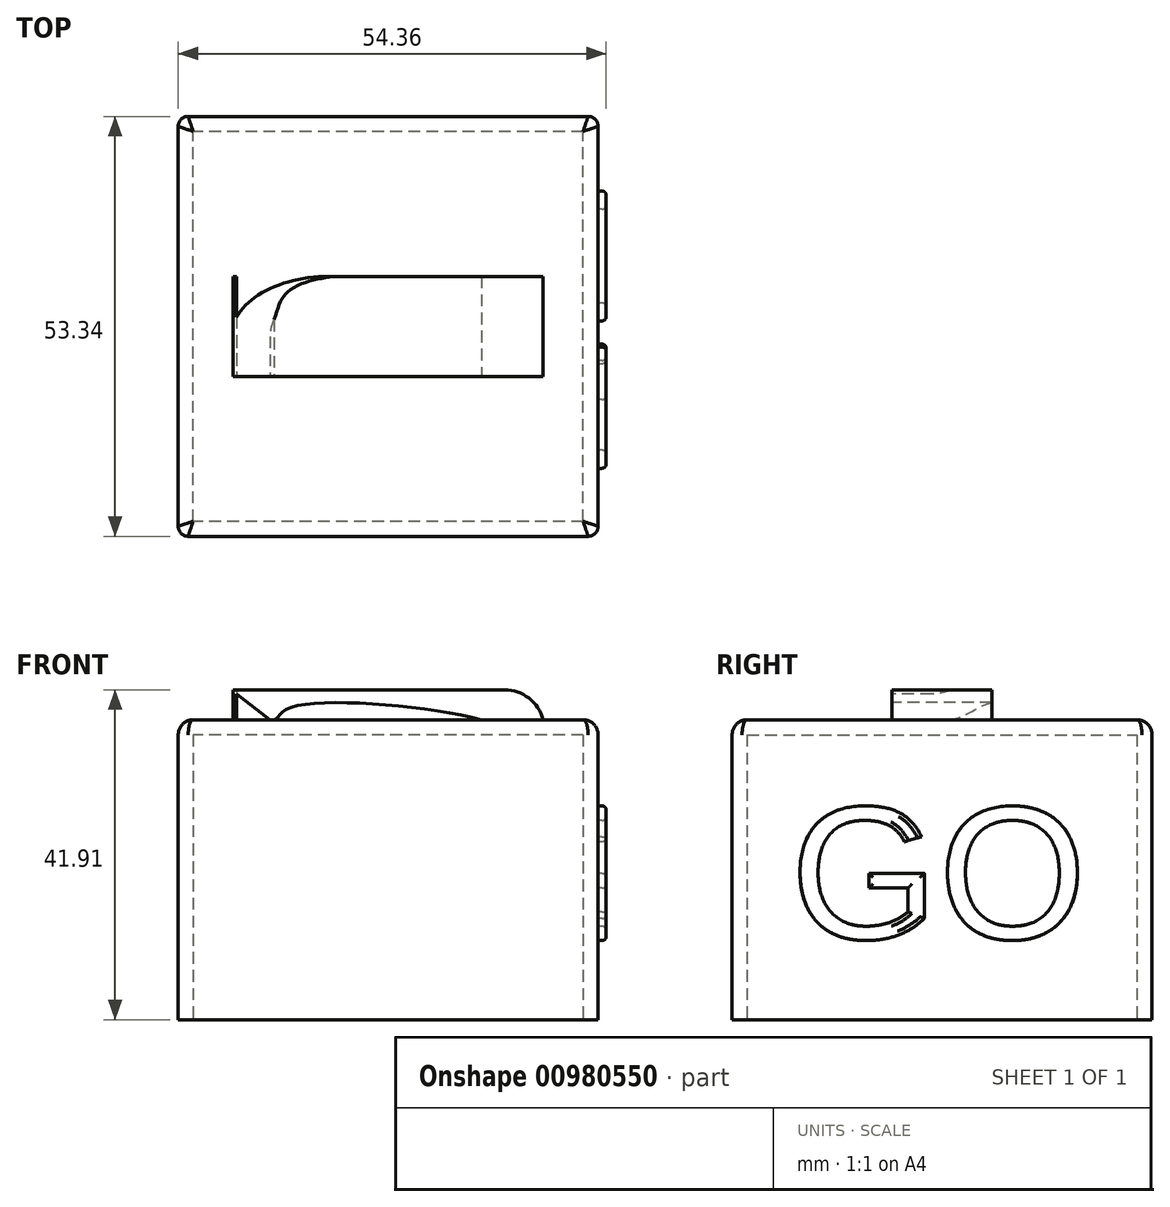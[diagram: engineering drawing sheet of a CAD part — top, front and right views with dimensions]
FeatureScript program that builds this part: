
annotation { "Feature Type Name" : "Feature", "Feature Type Description" : "" }
export const myFeature = defineFeature(function(context is Context, id is Id, definition is map)
    precondition{}
    {
        {
            var Q0;
            Q0=qCreatedBy(makeId("Top.planeOp"),FACE);
            var sketch = newSketch(context, id + "F0", { "sketchPlane" : qUnion([Q0])});
            skLineSegment(sketch, "E0.bottom", {"start": v(26.67, -26.67) * mm, "end": v(-26.67, -26.67) * mm});
            skLineSegment(sketch, "E0.top", {"start": v(26.67, 26.67) * mm, "end": v(-26.67, 26.67) * mm});
            skLineSegment(sketch, "E0.left", {"start": v(26.67, -26.67) * mm, "end": v(26.67, 26.67) * mm});
            skLineSegment(sketch, "E0.right", {"start": v(-26.67, -26.67) * mm, "end": v(-26.67, 26.67) * mm});
            skPoint(sketch, "E0.middle", {"position": v(0, 0) * mm});
            skSolve(sketch);
        }
        {
            var Q0;
            Q0=makeQuery(id+"F0.imprint","IMPRINT",FACE,{"disambiguationData":[TD([[makeQuery(id+"F0.imprint","IMPRINT",EDGE,{"derivedFrom":sQuery(id+"F0.wireOp",EDGE,"E0.bottom")}),-1.0]])]});
            extrude(context, id + "F1", {"entities" : qUnion([Q0]), "depth" : 38.1 * mm, "offsetDistance" : 25.4 * mm});
        }
        {
            var Q0;
            Q0=makeQuery(id+"F1.opExtrude","CAP_FACE",FACE,{"disambiguationData":[OSD([sQuery(id+"F0.wireOp",EDGE,"E0.bottom"),sQuery(id+"F0.wireOp",EDGE,"E0.top"),sQuery(id+"F0.wireOp",EDGE,"E0.left"),sQuery(id+"F0.wireOp",EDGE,"E0.right")])],"isStart":true});
            shell(context, id + "F2", {"entities" : qUnion([Q0]), "thickness" : 1.9 * mm});
        }
        {
            var Q0;
            Q0=makeQuery(id+"F1.opExtrude","SWEPT_EDGE",EDGE,{"disambiguationData":[OSD([sQuery(id+"F0.wireOp",EDGE,"E0.bottom"),sQuery(id+"F0.wireOp",EDGE,"E0.left")])]});
            var Q1;
            Q1=makeQuery(id+"F1.opExtrude","SWEPT_EDGE",EDGE,{"disambiguationData":[OSD([sQuery(id+"F0.wireOp",EDGE,"E0.top"),sQuery(id+"F0.wireOp",EDGE,"E0.left")])]});
            var Q2;
            Q2=makeQuery(id+"F1.opExtrude","SWEPT_EDGE",EDGE,{"disambiguationData":[OSD([sQuery(id+"F0.wireOp",EDGE,"E0.top"),sQuery(id+"F0.wireOp",EDGE,"E0.right")])]});
            var Q3;
            Q3=makeQuery(id+"F1.opExtrude","SWEPT_EDGE",EDGE,{"disambiguationData":[OSD([sQuery(id+"F0.wireOp",EDGE,"E0.bottom"),sQuery(id+"F0.wireOp",EDGE,"E0.right")])]});
            fillet(context, id + "F3", {"entities" : qUnion([Q0, Q1, Q2, Q3]), "radius" : 1.27 * mm, "tangentPropagation" : true, "allowEdgeOverflow" : false});
        }
        {
            var Q0;
            Q0=makeQuery(id+"F1.opExtrude","CAP_EDGE",EDGE,{"disambiguationData":[OSD([sQuery(id+"F0.wireOp",EDGE,"E0.right")])],"isStart":false});
            fillet(context, id + "F4", {"entities" : qUnion([Q0]), "radius" : 1.9 * mm, "tangentPropagation" : true, "allowEdgeOverflow" : false});
        }
        {
            var Q0;
            Q0=makeQuery(id+"F1.opExtrude","SWEPT_FACE",FACE,{"disambiguationData":[OSD([sQuery(id+"F0.wireOp",EDGE,"E0.left")])]});
            var sketch = newSketch(context, id + "F5", { "sketchPlane" : qUnion([Q0])});
            skText(sketch, "E1", { "text": "GO", "fontName": "Arimo-Regular.ttf"});
            const initialGuessF5  = {"E1": [-0.01925, 0.01028, 1, 0, 0.0174]};
            skSetInitialGuess(sketch, initialGuessF5);
            skSolve(sketch);
        }
        {
            var Q0;
            Q0 = qSketchRegion(id + "F5", true);
            extrude(context, id + "F6", {"entities" : qUnion([Q0]), "operationType" : NewBodyOperationType.ADD, "depth" : 1.02 * mm, "offsetDistance" : 25.4 * mm});
        }
        {
            var Q0;
            Q0=makeQuery(id+"F6.opExtrude","CAP_EDGE",EDGE,{"disambiguationData":[OSD([sQuery(id+"F5.wireOp",EDGE,"E1.sketch_text.stroke-0")])],"isStart":false});
            var Q1;
            Q1=makeQuery(id+"F6.opExtrude","CAP_EDGE",EDGE,{"disambiguationData":[OSD([sQuery(id+"F5.wireOp",EDGE,"E1.sketch_text.stroke-28")])],"isStart":false});
            var Q2;
            Q2=makeQuery(id+"F6.opExtrude","CAP_EDGE",EDGE,{"disambiguationData":[OSD([sQuery(id+"F5.wireOp",EDGE,"E1.sketch_text.stroke-8")])],"isStart":false});
            var Q3;
            Q3=makeQuery(id+"F6.opExtrude","CAP_EDGE",EDGE,{"disambiguationData":[OSD([sQuery(id+"F5.wireOp",EDGE,"E1.sketch_text.stroke-37")])],"isStart":false});
            var Q4;
            Q4=makeQuery(id+"F6.opExtrude","CAP_EDGE",EDGE,{"disambiguationData":[OSD([sQuery(id+"F5.wireOp",EDGE,"E1.sketch_text.stroke-14")])],"isStart":false});
            var Q5;
            Q5=makeQuery(id+"F6.opExtrude","CAP_EDGE",EDGE,{"disambiguationData":[OSD([sQuery(id+"F5.wireOp",EDGE,"E1.sketch_text.stroke-13")])],"isStart":false});
            var Q6;
            Q6=makeQuery(id+"F6.opExtrude","CAP_EDGE",EDGE,{"disambiguationData":[OSD([sQuery(id+"F5.wireOp",EDGE,"E1.sketch_text.stroke-17")])],"isStart":false});
            var Q7;
            Q7=makeQuery(id+"F6.opExtrude","CAP_EDGE",EDGE,{"disambiguationData":[OSD([sQuery(id+"F5.wireOp",EDGE,"E1.sketch_text.stroke-16")])],"isStart":false});
            var Q8;
            Q8=makeQuery(id+"F6.opExtrude","CAP_EDGE",EDGE,{"disambiguationData":[OSD([sQuery(id+"F5.wireOp",EDGE,"E1.sketch_text.stroke-15")])],"isStart":false});
            fillet(context, id + "F7", {"entities" : qUnion([Q0, Q1, Q2, Q3, Q4, Q5, Q6, Q7, Q8]), "radius" : 0.5 * mm, "tangentPropagation" : true, "allowEdgeOverflow" : false});
        }
        {
            var Q0;
            Q0=makeQuery(id+"F1.opExtrude","CAP_FACE",FACE,{"disambiguationData":[OSD([sQuery(id+"F0.wireOp",EDGE,"E0.bottom"),sQuery(id+"F0.wireOp",EDGE,"E0.top"),sQuery(id+"F0.wireOp",EDGE,"E0.left"),sQuery(id+"F0.wireOp",EDGE,"E0.right")])],"isStart":false});
            var sketch = newSketch(context, id + "F8", { "sketchPlane" : qUnion([Q0])});
            skLineSegment(sketch, "E2.bottom", {"start": v(-19.69, -6.35) * mm, "end": v(19.69, -6.35) * mm});
            skLineSegment(sketch, "E2.top", {"start": v(-19.69, 6.35) * mm, "end": v(19.69, 6.35) * mm});
            skLineSegment(sketch, "E2.left", {"start": v(-19.69, -6.35) * mm, "end": v(-19.69, 6.35) * mm});
            skLineSegment(sketch, "E2.right", {"start": v(19.69, -6.35) * mm, "end": v(19.69, 6.35) * mm});
            skPoint(sketch, "E2.middle", {"position": v(0, 0) * mm});
            skSolve(sketch);
        }
        {
            var Q0;
            Q0 = qSketchRegion(id + "F8", true);
            extrude(context, id + "F9", {"entities" : qUnion([Q0]), "operationType" : NewBodyOperationType.ADD, "depth" : 3.8 * mm, "offsetDistance" : 25.4 * mm});
        }
        {
            var Q0;
            Q0=makeQuery(id+"F9.opExtrude","CAP_EDGE",EDGE,{"disambiguationData":[OSD([sQuery(id+"F8.wireOp",EDGE,"E2.right")])],"isStart":false});
            fillet(context, id + "F10", {"entities" : qUnion([Q0]), "radius" : 5.08 * mm, "tangentPropagation" : true, "allowEdgeOverflow" : false});
        }
        {
            var Q0;
            Q0=makeQuery(id+"F9.opExtrude","SWEPT_FACE",FACE,{"disambiguationData":[OSD([sQuery(id+"F8.wireOp",EDGE,"E2.bottom")])]});
            var sketch = newSketch(context, id + "F11", { "sketchPlane" : qUnion([Q0])});
            skFitSpline(sketch, "E3", {"points": [v(-19.69, 40.83) * mm, v(-14.5, 38.1) * mm, v(-12.84, 39.47) * mm, v(11.87, 38.1) * mm], "startDerivative": vector(20.8, -15.14) * mm, "endDerivative": vector(37.16, -9.81) * mm});
            skLineSegment(sketch, "E4", {"start": v(-19.69, 40.83) * mm, "end": v(-19.69, 38.1) * mm});
            skLineSegment(sketch, "E5", {"start": v(-19.69, 38.1) * mm, "end": v(11.87, 38.1) * mm});
            skSolve(sketch);
        }
        {
            var Q0;
            {var subQ0=sQuery(id+"F11.wireOp",EDGE,"E5");var subQ1=sQuery(id+"F11.wireOp",EDGE,"E3");var subQ3=makeQuery(id+"F11.imprint","INTERSECT",VERTEX,{"disambiguationData":[OD(1.0)],"derivedFrom":[subQ1,subQ0]});Q0=makeQuery(id+"F11.imprint","IMPRINT",FACE,{"disambiguationData":[TD([[makeQuery(id+"F11.imprint","IMPRINT",EDGE,{"disambiguationData":[TD([[subQ3,-1.0]])],"derivedFrom":subQ1}),-1.0]])]});}
            extrude(context, id + "F12", {"entities" : qUnion([Q0]), "operationType" : NewBodyOperationType.REMOVE, "oppositeDirection" : true, "depth" : 25.4 * mm, "offsetDistance" : 25.4 * mm});
        }
        {
            var Q0;
            Q0=makeQuery(id+"F9.opExtrude","SWEPT_FACE",FACE,{"disambiguationData":[OSD([sQuery(id+"F8.wireOp",EDGE,"E2.bottom")])]});
            var sketch = newSketch(context, id + "F13", { "sketchPlane" : qUnion([Q0])});
            skLineSegment(sketch, "E6", {"start": v(-15, 38.1) * mm, "end": v(-19.25, 41.4) * mm});
            skLineSegment(sketch, "E7", {"start": v(-19.25, 41.4) * mm, "end": v(-19.25, 38.1) * mm});
            skLineSegment(sketch, "E8", {"start": v(-19.25, 38.1) * mm, "end": v(-15, 38.1) * mm});
            skSolve(sketch);
        }
        {
            var Q0;
            Q0=makeQuery(id+"F13.imprint","IMPRINT",FACE,{"disambiguationData":[TD([[makeQuery(id+"F13.imprint","IMPRINT",EDGE,{"derivedFrom":sQuery(id+"F13.wireOp",EDGE,"E6")}),1.0]])]});
            extrude(context, id + "F14", {"entities" : qUnion([Q0]), "operationType" : NewBodyOperationType.REMOVE, "oppositeDirection" : true, "depth" : 25.4 * mm, "offsetDistance" : 25.4 * mm});
        }
        {
            var Q0;
            Q0=makeQuery(id+"F14.boolean.opBoolean","COPY",EDGE,{"derivedFrom":makeQuery(id+"F14.opExtrude","CAP_EDGE",EDGE,{"disambiguationData":[OSD([sQuery(id+"F13.wireOp",EDGE,"E6")])],"isStart":true})});
            var Q1;
            Q1=makeQuery(id+"F14.boolean.opBoolean","INTERSECT",EDGE,{"derivedFrom":[makeQuery(id+"F9.opExtrude","SWEPT_FACE",FACE,{"disambiguationData":[OSD([sQuery(id+"F8.wireOp",EDGE,"E2.top")])]}),makeQuery(id+"F14.opExtrude","SWEPT_FACE",FACE,{"disambiguationData":[OSD([sQuery(id+"F13.wireOp",EDGE,"E6")])]})]});
            fillet(context, id + "F15", {"entities" : qUnion([Q0, Q1]), "radius" : 7.62 * mm, "tangentPropagation" : true, "allowEdgeOverflow" : false});
        }
    });
